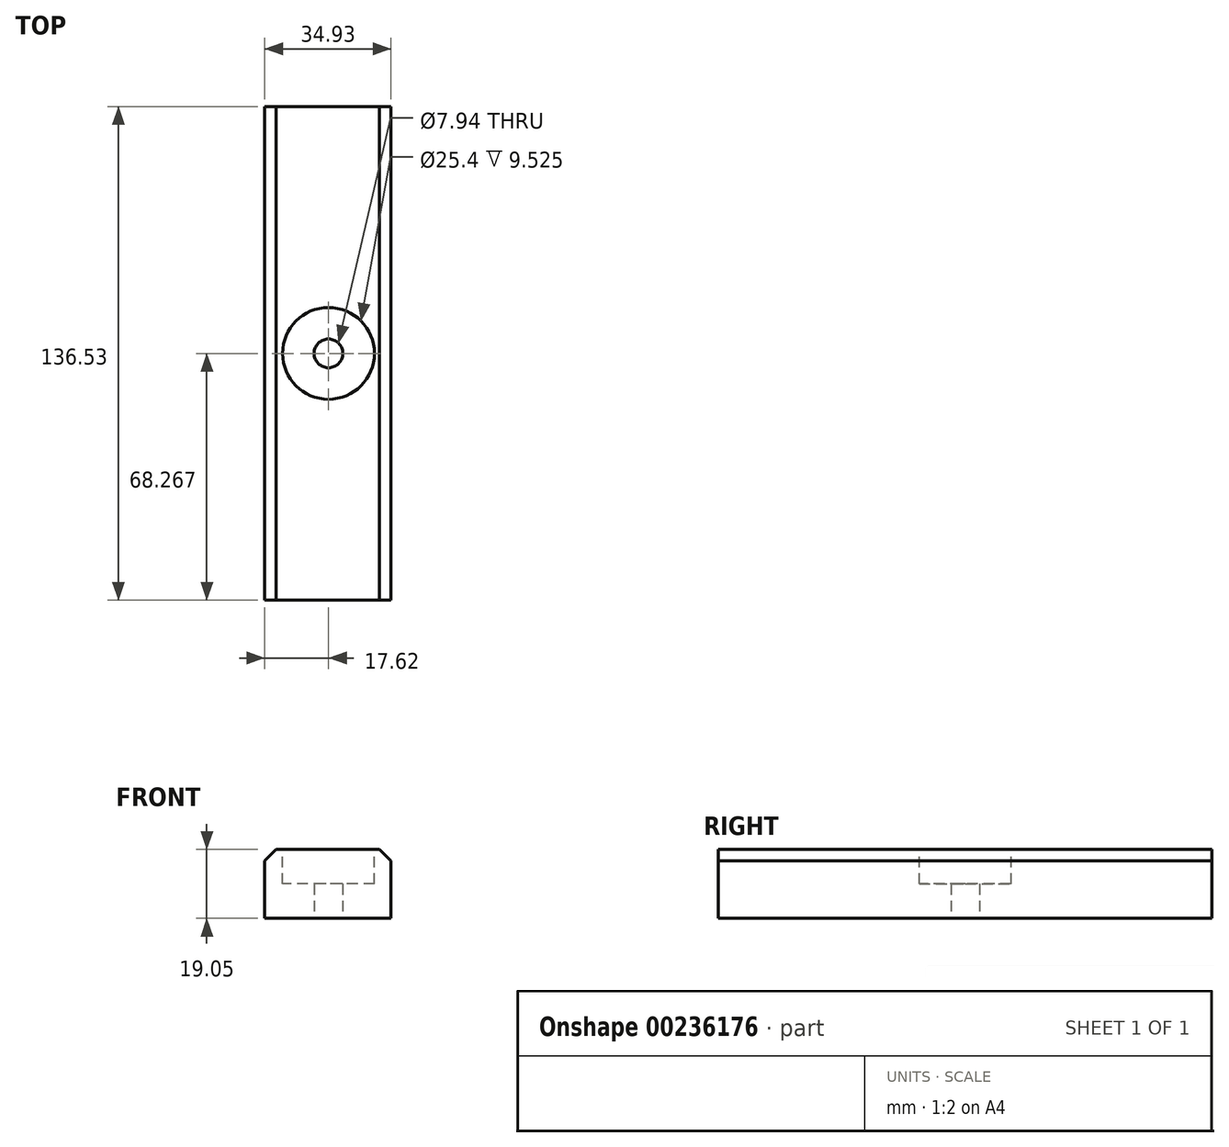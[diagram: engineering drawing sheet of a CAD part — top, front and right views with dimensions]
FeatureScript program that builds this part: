
annotation { "Feature Type Name" : "Feature", "Feature Type Description" : "" }
export const myFeature = defineFeature(function(context is Context, id is Id, definition is map)
    precondition{}
    {
        {
            var Q0;
            Q0=qCreatedBy(makeId("Top.planeOp"),FACE);
            var sketch = newSketch(context, id + "F0", { "sketchPlane" : qUnion([Q0])});
            skLineSegment(sketch, "E0.bottom", {"start": v(-17.62, 106.92) * mm, "end": v(17.3, 106.92) * mm});
            skLineSegment(sketch, "E0.top", {"start": v(-17.62, -29.6) * mm, "end": v(17.3, -29.6) * mm});
            skLineSegment(sketch, "E0.left", {"start": v(-17.62, 106.92) * mm, "end": v(-17.62, -29.6) * mm});
            skLineSegment(sketch, "E0.right", {"start": v(17.3, 106.92) * mm, "end": v(17.3, -29.6) * mm});
            skSolve(sketch);
        }
        {
            var Q0;
            Q0=makeQuery(id+"F0.imprint","IMPRINT",FACE,{"disambiguationData":[TD([[makeQuery(id+"F0.imprint","IMPRINT",EDGE,{"derivedFrom":sQuery(id+"F0.wireOp",EDGE,"E0.bottom")}),-1.0]])]});
            extrude(context, id + "F1", {"entities" : qUnion([Q0]), "depth" : 19.05 * mm});
        }
        {
            var Q0;
            Q0=makeQuery(id+"F1.opExtrude","CAP_EDGE",EDGE,{"disambiguationData":[OSD([sQuery(id+"F0.wireOp",EDGE,"E0.right")])],"isStart":false});
            var Q1;
            Q1=makeQuery(id+"F1.opExtrude","CAP_EDGE",EDGE,{"disambiguationData":[OSD([sQuery(id+"F0.wireOp",EDGE,"E0.left")])],"isStart":false});
            chamfer(context, id + "F2", {"entities" : qUnion([Q0, Q1]), "width" : 3.17 * mm, "tangentPropagation" : true});
        }
        {
            var Q0;
            Q0=makeQuery(id+"F1.opExtrude","CAP_FACE",FACE,{"disambiguationData":[OSD([sQuery(id+"F0.wireOp",EDGE,"E0.bottom"),sQuery(id+"F0.wireOp",EDGE,"E0.top"),sQuery(id+"F0.wireOp",EDGE,"E0.left"),sQuery(id+"F0.wireOp",EDGE,"E0.right")])],"isStart":false});
            var sketch = newSketch(context, id + "F3", { "sketchPlane" : qUnion([Q0])});
            skCircle(sketch, "E1", {"center": v(0, 38.66) * mm, "radius": 12.7 * mm});
            skPoint(sketch, "E1.centerSnap0", {"position": v(14.13, 38.66) * mm});
            skSolve(sketch);
        }
        {
            var Q0;
            Q0=makeQuery(id+"F3.imprint","IMPRINT",FACE,{"disambiguationData":[TD([[makeQuery(id+"F3.imprint","IMPRINT",EDGE,{"derivedFrom":sQuery(id+"F3.wireOp",EDGE,"E1")}),1.0]])]});
            extrude(context, id + "F4", {"entities" : qUnion([Q0]), "operationType" : NewBodyOperationType.ADD, "oppositeDirection" : true, "depth" : 9.52 * mm});
        }
        {
            var Q0;
            Q0=makeQuery(id+"F1.opExtrude","CAP_FACE",FACE,{"disambiguationData":[OSD([sQuery(id+"F0.wireOp",EDGE,"E0.bottom"),sQuery(id+"F0.wireOp",EDGE,"E0.top"),sQuery(id+"F0.wireOp",EDGE,"E0.left"),sQuery(id+"F0.wireOp",EDGE,"E0.right")])],"isStart":true});
            var sketch = newSketch(context, id + "F5", { "sketchPlane" : qUnion([Q0])});
            skCircle(sketch, "E2", {"center": v(0, -38.66) * mm, "radius": 3.97 * mm});
            skPoint(sketch, "E2.centerSnap0", {"position": v(17.3, -38.66) * mm});
            skSolve(sketch);
        }
        {
            var Q0;
            Q0=makeQuery(id+"F5.imprint","IMPRINT",FACE,{"disambiguationData":[TD([[makeQuery(id+"F5.imprint","IMPRINT",EDGE,{"derivedFrom":sQuery(id+"F5.wireOp",EDGE,"E2")}),1.0]])]});
            var Q1;
            Q1=sQuery(id+"F5.wireOp",EDGE,"E2");
            extrude(context, id + "F6", {"entities" : qUnion([Q0]), "operationType" : NewBodyOperationType.REMOVE, "surfaceEntities" : qUnion([Q1]), "endBound" : BoundingType.THROUGH_ALL, "oppositeDirection" : true, "depth" : 23.88 * mm});
        }
        {
            var Q0;
            Q0=makeQuery(id+"F3.imprint","IMPRINT",FACE,{"disambiguationData":[TD([[makeQuery(id+"F3.imprint","IMPRINT",EDGE,{"derivedFrom":sQuery(id+"F3.wireOp",EDGE,"E1")}),1.0]])]});
            extrude(context, id + "F7", {"entities" : qUnion([Q0]), "operationType" : NewBodyOperationType.REMOVE, "oppositeDirection" : true, "depth" : 9.52 * mm});
        }
    });
